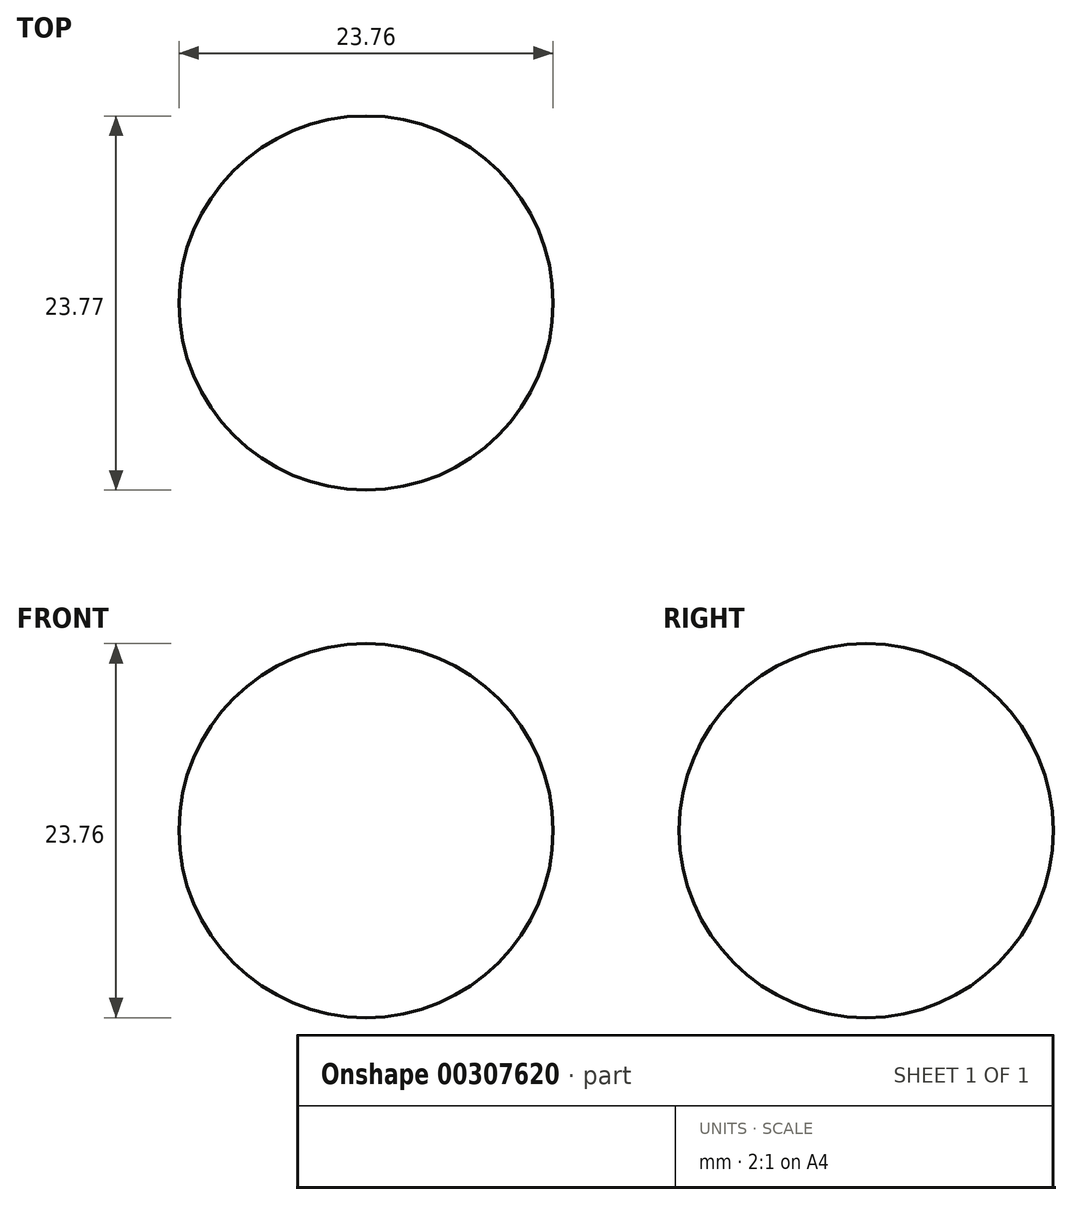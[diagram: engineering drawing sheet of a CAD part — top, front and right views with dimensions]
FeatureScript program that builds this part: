
annotation { "Feature Type Name" : "Feature", "Feature Type Description" : "" }
export const myFeature = defineFeature(function(context is Context, id is Id, definition is map)
    precondition{}
    {
        {
            var Q0;
            Q0=qCreatedBy(makeId("Top.planeOp"),FACE);
            var sketch = newSketch(context, id + "F0", { "sketchPlane" : qUnion([Q0])});
            skArc(sketch, "E0", {"start": v(14.59, -0.07) * mm, "mid": v(39.3, 44.6) * mm, "end": v(0, 77.17) * mm});
            skArc(sketch, "E1", {"start": v(0, -1.33) * mm, "mid": v(38.5, 37.17) * mm, "end": v(0, 75.67) * mm});
            skLineSegment(sketch, "E2", {"start": v(0, 77.17) * mm, "end": v(0, 75.67) * mm});
            skLineSegment(sketch, "E3.trimOffspring", {"start": v(0, -1.33) * mm, "end": v(0, -2.83) * mm});
            skLineSegment(sketch, "E4", {"start": v(0, 0) * mm, "end": v(20.81, -0.1) * mm, "construction": true});
            skSolve(sketch);
        }
        {
            var Q0;
            Q0=qCreatedBy(makeId("Top.planeOp"),FACE);
            var sketch = newSketch(context, id + "F1", { "sketchPlane" : qUnion([Q0])});
            skLineSegment(sketch, "E5", {"start": v(0, 77.54) * mm, "end": v(0, -55.92) * mm, "construction": true});
            skLineSegment(sketch, "E6", {"start": v(16.7, 0) * mm, "end": v(16.7, -55.92) * mm, "construction": true});
            skLineSegment(sketch, "E7", {"start": v(16.7, -55.92) * mm, "end": v(0, -55.92) * mm, "construction": true});
            skLineSegment(sketch, "E8", {"start": v(16.7, 0) * mm, "end": v(0, 0) * mm, "construction": true});
            skSolve(sketch);
        }
        {
            var Q0;
            Q0=qCreatedBy(makeId("Top.planeOp"),FACE);
            var sketch = newSketch(context, id + "F2", { "sketchPlane" : qUnion([Q0])});
            skFitSpline(sketch, "E9", {"points": [v(16.49, 0) * mm, v(14.43, -24.82) * mm, v(3.1, -35.32) * mm, v(8.87, -52.62) * mm, v(0, -55.71) * mm], "startDerivative": vector(12.04, -94.77) * mm, "endDerivative": vector(-67.56, -3.24) * mm});
            skSolve(sketch);
        }
        {
            var Q0;
            Q0=sQuery(id+"F0.wireOp",EDGE,"E0");
            var Q1;
            Q1=sQuery(id+"F2.wireOp",EDGE,"E9");
            var Q2;
            Q2=sQuery(id+"F1.wireOp",EDGE,"E5");
            revolve(context, id + "F3", {"bodyType" : ToolBodyType.SURFACE, "surfaceEntities" : qUnion([Q0, Q1]), "axis" : qUnion([Q2]), "revolveType" : RevolveType.FULL});
        }
        {
            var Q0;
            Q0=qCreatedBy(makeId("Top.planeOp"),FACE);
            var sketch = newSketch(context, id + "F4", { "sketchPlane" : qUnion([Q0])});
            skArc(sketch, "E10", {"start": v(0, 49.8) * mm, "mid": v(11.88, 61.69) * mm, "end": v(0, 73.57) * mm});
            skLineSegment(sketch, "E11", {"start": v(0, 73.57) * mm, "end": v(0, 49.8) * mm});
            skSolve(sketch);
        }
        {
            var Q0;
            Q0 = qSketchRegion(id + "F4", true);
            var Q1;
            Q1=sQuery(id+"F1.wireOp",EDGE,"E5");
            revolve(context, id + "F5", {"entities" : qUnion([Q0]), "axis" : qUnion([Q1]), "revolveType" : RevolveType.FULL});
        }
        {
            var Q0;
            Q0=qCreatedBy(makeId("Right.planeOp"),FACE);
            var sketch = newSketch(context, id + "F6", { "sketchPlane" : qUnion([Q0])});
            skLineSegment(sketch, "E12.bottom", {"start": v(11, 58.68) * mm, "end": v(17.08, 58.68) * mm});
            skLineSegment(sketch, "E12.top", {"start": v(11, -48.14) * mm, "end": v(17.08, -48.14) * mm});
            skLineSegment(sketch, "E12.left", {"start": v(11, 58.68) * mm, "end": v(11, 23) * mm});
            skLineSegment(sketch, "E12.right", {"start": v(17.08, 58.68) * mm, "end": v(17.08, 23) * mm});
            skLineSegment(sketch, "E13.bottom", {"start": v(36.54, 60.91) * mm, "end": v(43.23, 60.91) * mm});
            skLineSegment(sketch, "E13.top", {"start": v(36.54, -49.36) * mm, "end": v(43.23, -49.36) * mm});
            skLineSegment(sketch, "E13.left", {"start": v(36.54, 60.91) * mm, "end": v(36.54, 23) * mm});
            skLineSegment(sketch, "E13.right", {"start": v(43.23, 60.91) * mm, "end": v(43.23, 23) * mm});
            skLineSegment(sketch, "E14.bottom", {"start": v(11, 23) * mm, "end": v(17.08, 23) * mm});
            skLineSegment(sketch, "E14.top", {"start": v(11, -18.95) * mm, "end": v(17.08, -18.95) * mm});
            skLineSegment(sketch, "E15.trimOffspring", {"start": v(11, -18.95) * mm, "end": v(11, -48.14) * mm});
            skLineSegment(sketch, "E16.trimOffspring", {"start": v(17.08, -18.95) * mm, "end": v(17.08, -48.14) * mm});
            skLineSegment(sketch, "E17.trimOffspring", {"start": v(36.54, 23) * mm, "end": v(43.23, 23) * mm});
            skLineSegment(sketch, "E18.trimOffspring", {"start": v(36.54, -18.95) * mm, "end": v(43.23, -18.95) * mm});
            skLineSegment(sketch, "E19.trimOffspring", {"start": v(36.54, -18.95) * mm, "end": v(36.54, -49.36) * mm});
            skLineSegment(sketch, "E20.trimOffspring", {"start": v(43.23, -18.95) * mm, "end": v(43.23, -49.36) * mm});
            skSolve(sketch);
        }
        {
            var Q0;
            Q0=makeQuery(id+"F6.imprint","IMPRINT",FACE,{"disambiguationData":[TD([[makeQuery(id+"F6.imprint","IMPRINT",EDGE,{"derivedFrom":sQuery(id+"F6.wireOp",EDGE,"E12.bottom")}),-1.0]])]});
            extrude(context, id + "F7", {"entities" : qUnion([Q0]), "operationType" : NewBodyOperationType.REMOVE, "endBound" : BoundingType.SYMMETRIC, "oppositeDirection" : true, "depth" : 79 * mm});
        }
    });
